# Revit family: Faucet-Symmons-Dia-Kitchen-Single_Handle-Pull_Down
name_source: partatom
category: Plumbing Fixtures
revit_build: Autodesk Revit 2015 (Build: 20140606_1530(x64)
units: mm (PartAtom-declared; Revit-internal decimal feet)

## types (2) — shared parameters
Date Modified = January 30, 2015
Equipment Abbreviation = KF
Family Version = 1.0
Gallons Per Minute = 2.200 GPM
Manufacturer = Symmons Industries, Inc.
Model Disclaimer = Contact Symmons Industries, Inc. For More Information
Product Documentation Link = http://www.symmons.com
Product Page URL = http://www.symmons.com
Product data url = https://bimobject.com
URL = http://www.symmons.com
z 0.5 Flow Rate Restrictor = No
z 1.5 Flow Rate Restrictor = No
z Error = No
z Flow Rate Restrictor Selection = No Selection
z GPM GPM = 1.000 GPM
z GPM Number = 2.2
z Type GPM = 2.2
z Visibility = Yes
zero-valued in all types: z Error Type, z Type Flow Restrictior

## per-type parameters (varying)
| type | Description | Model | Product Material | z Type |
| 2.2 GPM Flow Restrictor, Chrome | Single Handle Pull-Down Kitchen Faucet, 2.2 Flow Rate Restrictor, Chrome | SPP-3510 | Chrome - Symmons - Polished | 1 |
| 2.2 GPM Flow Restrictor, Satin Nickel | Single Handle Pull-Down Kitchen Faucet, 2.2 Flow Rate Restrictor, Satin Nickel | SPP-3510-STN | Nickel - Symmons - Satin | 2 |

## geometry (parser evidence)
native form markers: Blend x8, Sweep x3
no freeform markers — native parametric forms only
